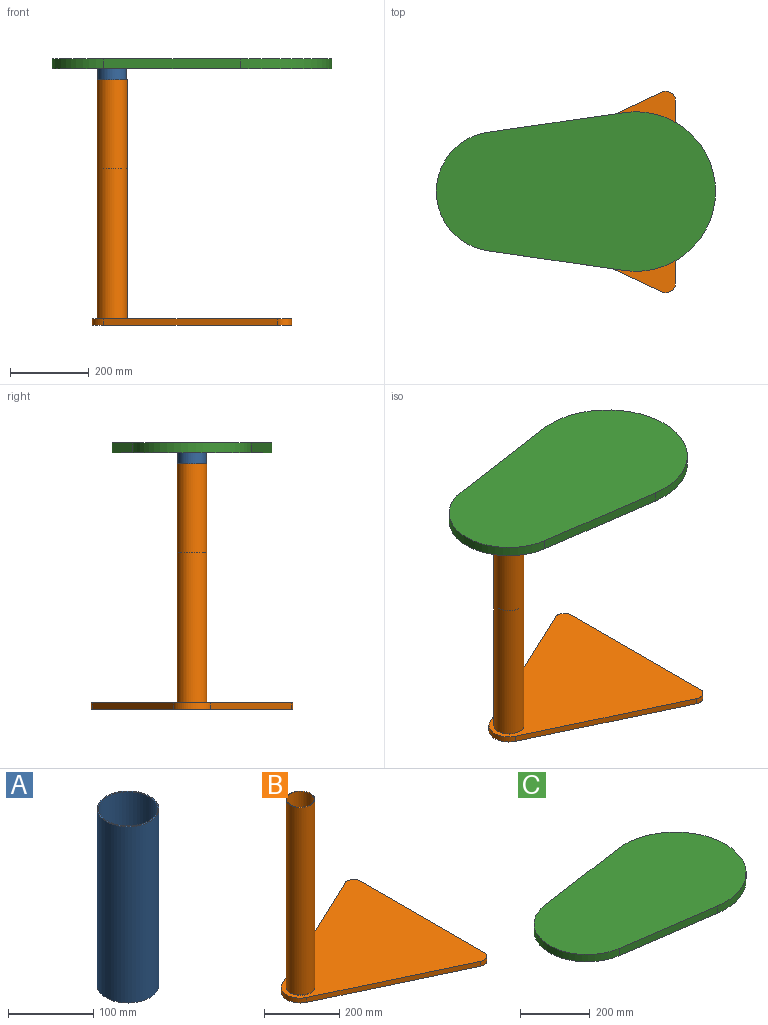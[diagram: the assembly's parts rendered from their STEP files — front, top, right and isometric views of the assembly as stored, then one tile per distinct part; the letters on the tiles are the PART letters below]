
ASSEMBLY  parts=3 mates=2
PART A: 4 faces, bbox 72.8x72.8x254 mm
  f0: cylinder r=34.8mm len=254mm, axis (0,0,-1), area 55535.1mm2, adj f2,f3
  f1: cylinder r=36.39mm len=254mm, axis (0,0,-1), area 58068.7mm2, adj f2,f3
  f2: plane 72.77x72.77mm, normal (0,0,1), area 355mm2, adj f0,f1
  f3: plane 72.77x72.77mm, normal (0,0,-1), area 355mm2, adj f0,f1
PART B: 12 faces, bbox 508x512.8x625.5 mm
  f0: cylinder r=25.4mm len=36.2mm, axis (0,0,-1), area 810.5mm2, adj f1,f5,f6,f7
  f1: plane 442.6x208.03mm, normal (-0.43,0.91,0), area 7763.7mm2, adj f0,f2,f6,f7
  f2: cylinder r=50.8mm len=91.95mm, axis (0,0,-1), area 1824.9mm2, adj f1,f3,f6,f7
  f3: plane 442.6x208.03mm, normal (-0.43,-0.91,0), area 7763.7mm2, adj f2,f4,f6,f7
  f4: cylinder r=25.4mm len=36.2mm, axis (0,0,-1), area 810.5mm2, adj f3,f5,f6,f7
  f5: plane 462.03x15.88mm, normal (1,0,0), area 7334.6mm2, adj f0,f4,f6,f7
  f6: plane 512.83x508mm, normal (0,0,1), area 148408.8mm2, adj f0,f1,f2,f3,f4,f5,f9
  f7: plane 512.83x508mm, normal (0,0,-1), area 152969.1mm2, adj f0,f1,f2,f3,f4,f5
  f8: cylinder r=36.51mm len=609.6mm, axis (0,0,-1), area 139851.3mm2, adj f10,f11
  f9: cylinder r=38.1mm len=609.6mm, axis (0,0,-1), area 145931.8mm2, adj f6,f10
  f10: plane 76.2x76.2mm, normal (0,0,1), area 372.1mm2, adj f8,f9
  f11: plane 73.03x73.03mm, normal (0,0,1), area 4188.3mm2, adj f8
PART C: 6 faces, bbox 711.2x406.4x25.4 mm
  f0: plane 348.34x50.28mm, normal (-0.14,-0.99,0), area 8939.6mm2, adj f1,f3,f4,f5
  f1: cylinder r=203.2mm len=406.4mm, axis (0,0,-1), area 17694.4mm2, adj f0,f2,f4,f5
  f2: plane 348.34x50.28mm, normal (-0.14,0.99,0), area 8939.6mm2, adj f1,f3,f4,f5
  f3: cylinder r=152.4mm len=301.67mm, axis (0,0,-1), area 11051.2mm2, adj f0,f2,f4,f5
  f4: plane 711.2x406.4mm, normal (0,0,1), area 229085.4mm2, adj f0,f1,f2,f3
  f5: plane 711.2x406.4mm, normal (0,0,-1), area 229085.4mm2, adj f0,f1,f2,f3
PLACE A t=(-1705.87,-722.62,-482.23)mm
PLACE B t=(-1705.87,-722.62,-255.68)mm
PLACE C rot(axis=(1,0,0),180deg) t=(-1025.24,-1179.35,422.64)mm
MATE cylindrical B.f2 <-> A.f0  axis (0,0,1) through (-1351.81,-809.58,369.79)mm
MATE fastened A.f0 <-> C.f3  axis (0,0,-1) through (-1351.81,-809.58,397.24)mm
